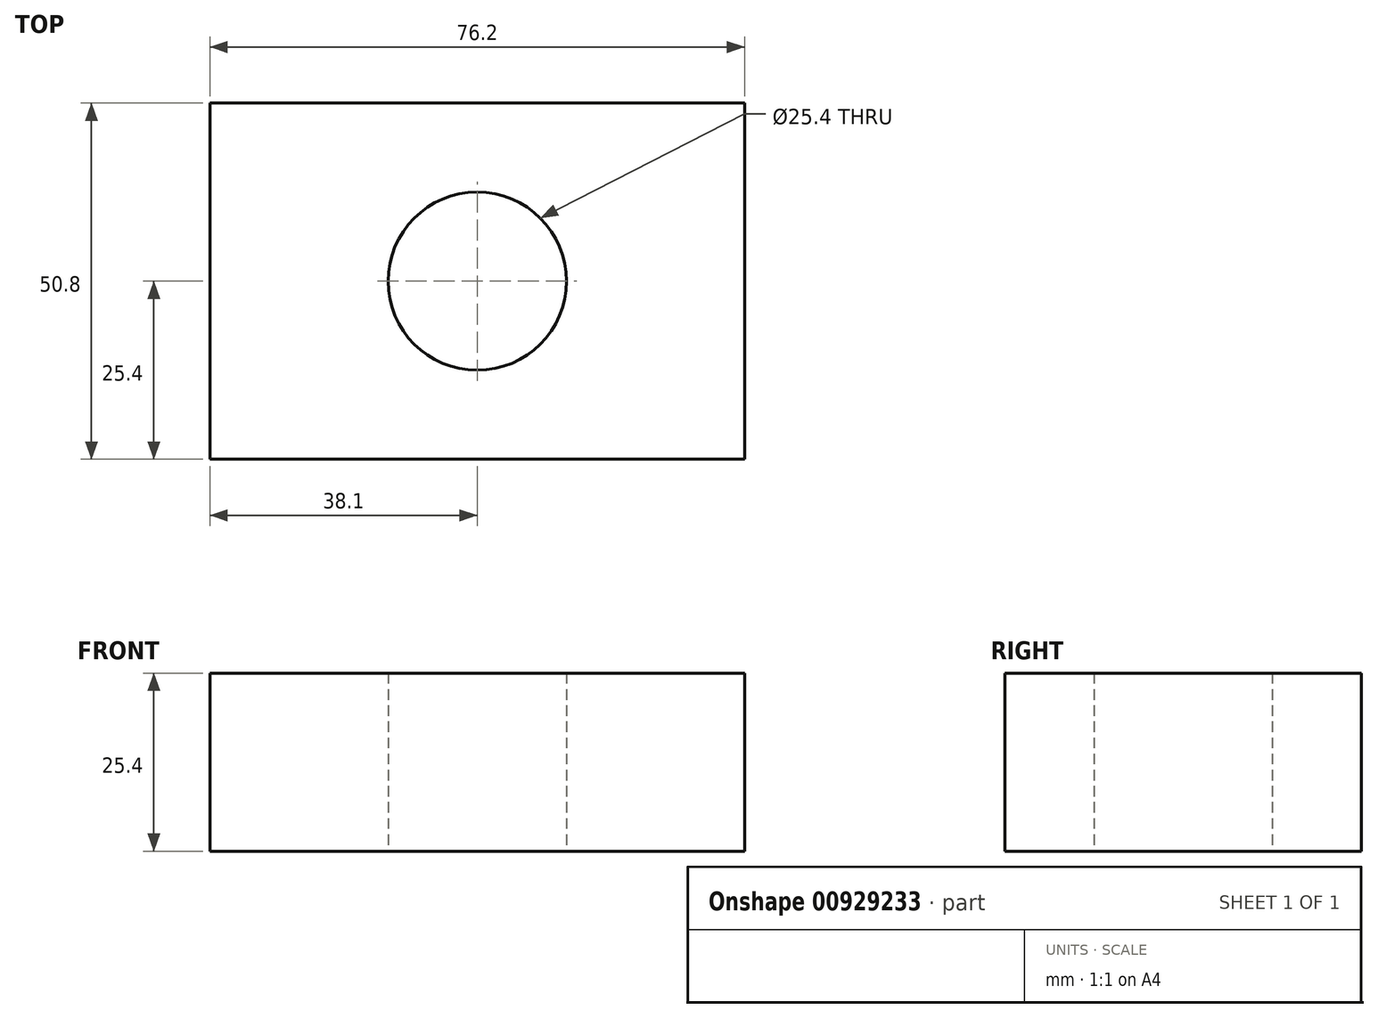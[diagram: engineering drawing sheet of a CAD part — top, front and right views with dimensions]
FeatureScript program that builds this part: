
annotation { "Feature Type Name" : "Feature", "Feature Type Description" : "" }
export const myFeature = defineFeature(function(context is Context, id is Id, definition is map)
    precondition{}
    {
        {
            var Q0;
            Q0=qCreatedBy(makeId("Top.planeOp"),FACE);
            var sketch = newSketch(context, id + "F0", { "sketchPlane" : qUnion([Q0])});
            skLineSegment(sketch, "E0.bottom", {"start": v(38.1, -25.4) * mm, "end": v(-38.1, -25.4) * mm});
            skLineSegment(sketch, "E0.top", {"start": v(38.1, 25.4) * mm, "end": v(-38.1, 25.4) * mm});
            skLineSegment(sketch, "E0.left", {"start": v(38.1, -25.4) * mm, "end": v(38.1, 25.4) * mm});
            skLineSegment(sketch, "E0.right", {"start": v(-38.1, -25.4) * mm, "end": v(-38.1, 25.4) * mm});
            skPoint(sketch, "E0.middle", {"position": v(0, 0) * mm});
            skCircle(sketch, "E1", {"center": v(0, 0) * mm, "radius": 12.7 * mm});
            skSolve(sketch);
        }
        {
            var Q0;
            Q0=makeQuery(id+"F0.imprint","IMPRINT",FACE,{"disambiguationData":[TD([[makeQuery(id+"F0.imprint","IMPRINT",EDGE,{"derivedFrom":sQuery(id+"F0.wireOp",EDGE,"E0.bottom")}),-1.0]])]});
            extrude(context, id + "F1", {"entities" : qUnion([Q0]), "depth" : 25.4 * mm, "offsetDistance" : 25.4 * mm});
        }
    });
